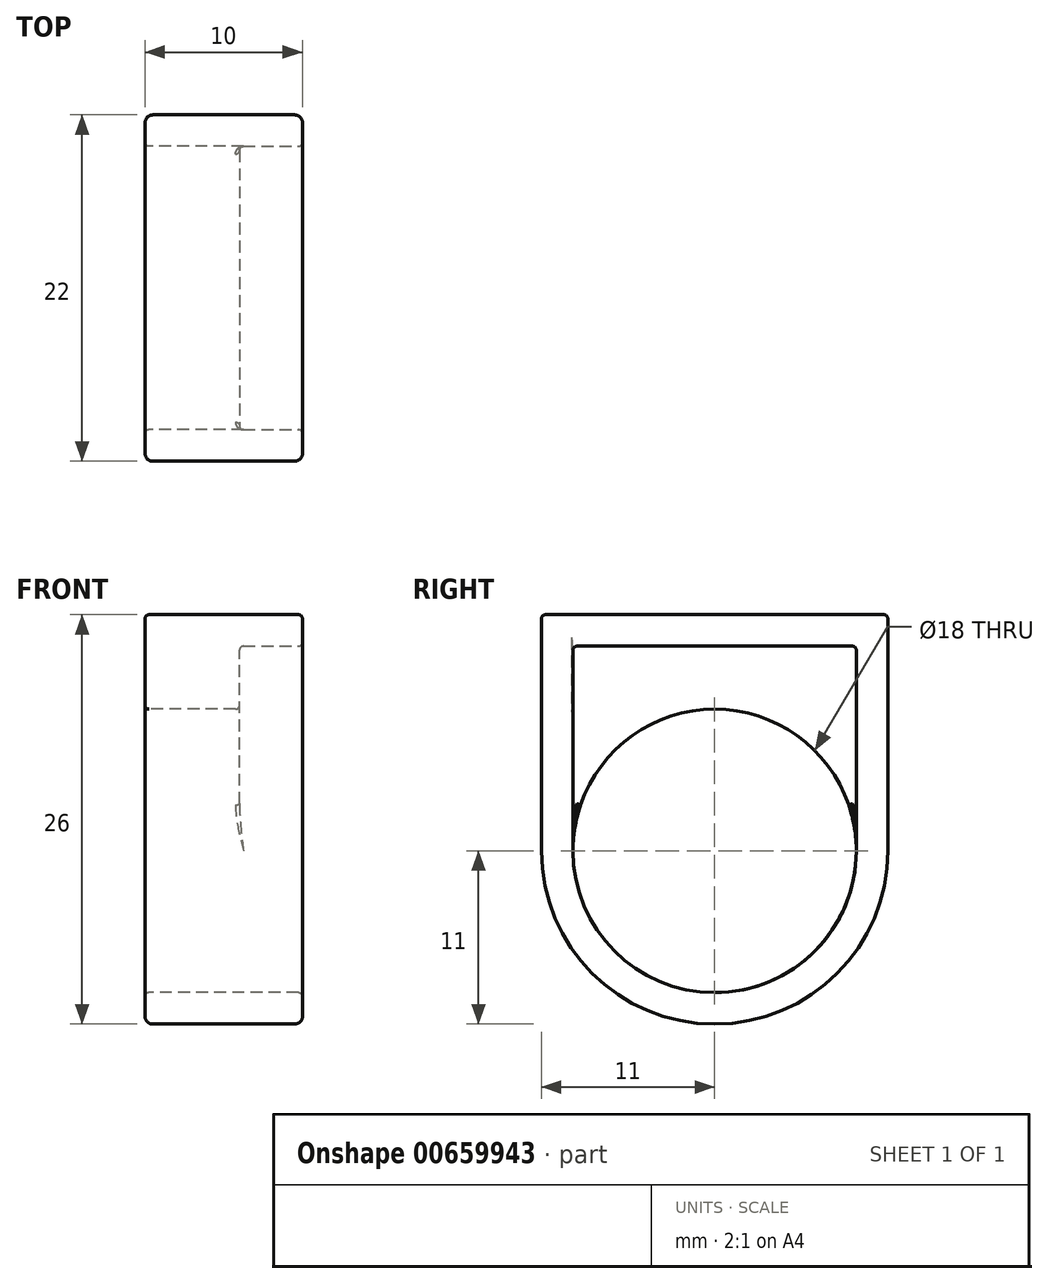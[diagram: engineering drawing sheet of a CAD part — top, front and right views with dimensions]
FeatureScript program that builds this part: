
annotation { "Feature Type Name" : "Feature", "Feature Type Description" : "" }
export const myFeature = defineFeature(function(context is Context, id is Id, definition is map)
    precondition{}
    {
        {
            var Q0;
            Q0=qCreatedBy(makeId("Right.planeOp"),FACE);
            var sketch = newSketch(context, id + "F0", { "sketchPlane" : qUnion([Q0])});
            skCircle(sketch, "E0", {"center": v(0, 0) * mm, "radius": 9 * mm});
            skArc(sketch, "E1", {"start": v(-11, 0) * mm, "mid": v(0, -11) * mm, "end": v(11, 0) * mm});
            skLineSegment(sketch, "E2", {"start": v(11, 0) * mm, "end": v(11, 15) * mm});
            skLineSegment(sketch, "E3", {"start": v(-11, 0) * mm, "end": v(-11, 15) * mm});
            skLineSegment(sketch, "E4", {"start": v(-11, 15) * mm, "end": v(11, 15) * mm});
            skSolve(sketch);
        }
        {
            var Q0;
            Q0 = qSketchRegion(id + "F0", true);
            extrude(context, id + "F1", {"entities" : qUnion([Q0]), "endBound" : BoundingType.SYMMETRIC, "depth" : 10 * mm, "offsetDistance" : 25 * mm});
        }
        {
            var Q0;
            Q0=makeQuery(id+"F1.opExtrude","CAP_FACE",FACE,{"disambiguationData":[OSD([sQuery(id+"F0.wireOp",EDGE,"E0"),sQuery(id+"F0.wireOp",EDGE,"E1"),sQuery(id+"F0.wireOp",EDGE,"E2"),sQuery(id+"F0.wireOp",EDGE,"E3"),sQuery(id+"F0.wireOp",EDGE,"E4")])],"isStart":false});
            var sketch = newSketch(context, id + "F2", { "sketchPlane" : qUnion([Q0])});
            skLineSegment(sketch, "E5.0", {"start": v(9, 13) * mm, "end": v(-9, 13) * mm});
            skLineSegment(sketch, "E5.1", {"start": v(9, 0) * mm, "end": v(9, 13) * mm});
            skArc(sketch, "E5.2", {"start": v(-9, 0) * mm, "mid": v(0, -9) * mm, "end": v(9, 0) * mm});
            skLineSegment(sketch, "E5.3", {"start": v(-9, 13) * mm, "end": v(-9, 0) * mm});
            skSolve(sketch);
        }
        {
            var Q0;
            Q0 = qSketchRegion(id + "F2", true);
            extrude(context, id + "F3", {"entities" : qUnion([Q0]), "operationType" : NewBodyOperationType.REMOVE, "endBound" : BoundingType.SYMMETRIC, "oppositeDirection" : true, "depth" : 8 * mm, "offsetDistance" : 25 * mm});
        }
        {
            var Q0;
            Q0=makeQuery(id+"F1.opExtrude","CAP_EDGE",EDGE,{"disambiguationData":[OSD([sQuery(id+"F0.wireOp",EDGE,"E3")])],"isStart":false});
            var Q1;
            Q1=makeQuery(id+"F1.opExtrude","CAP_EDGE",EDGE,{"disambiguationData":[OSD([sQuery(id+"F0.wireOp",EDGE,"E3")])],"isStart":true});
            fillet(context, id + "F4", {"entities" : qUnion([Q0, Q1]), "radius" : 0.5 * mm, "tangentPropagation" : true, "allowEdgeOverflow" : false});
        }
        {
            var Q0;
            Q0=makeQuery(id+"F1.opExtrude","CAP_EDGE",EDGE,{"disambiguationData":[OSD([sQuery(id+"F0.wireOp",EDGE,"E0")])],"isStart":false});
            var Q1;
            Q1=makeQuery(id+"F1.opExtrude","SWEPT_EDGE",EDGE,{"disambiguationData":[OSD([sQuery(id+"F0.wireOp",EDGE,"E1"),sQuery(id+"F0.wireOp",EDGE,"E3")])]});
            var Q2;
            Q2=makeQuery(id+"F3.boolean.opBoolean","INTERSECT",EDGE,{"derivedFrom":[makeQuery(id+"F1.opExtrude","CAP_FACE",FACE,{"disambiguationData":[OSD([sQuery(id+"F0.wireOp",EDGE,"E0"),sQuery(id+"F0.wireOp",EDGE,"E1"),sQuery(id+"F0.wireOp",EDGE,"E2"),sQuery(id+"F0.wireOp",EDGE,"E3"),sQuery(id+"F0.wireOp",EDGE,"E4")])],"isStart":false}),makeQuery(id+"F3.opExtrude","SWEPT_FACE",FACE,{"disambiguationData":[OSD([sQuery(id+"F2.wireOp",EDGE,"E5.0")])]})]});
            var Q3;
            {var subQ0=sQuery(id+"F0.wireOp",EDGE,"E1");Q3=makeQuery(id+"F4.opFillet","BLEND_EDGE",EDGE,{"blendedFrom":[makeQuery(id+"F1.opExtrude","CAP_EDGE",EDGE,{"disambiguationData":[OSD([subQ0])],"isStart":false}),makeQuery(id+"F1.opExtrude","CAP_FACE",FACE,{"disambiguationData":[OSD([sQuery(id+"F0.wireOp",EDGE,"E0"),subQ0,sQuery(id+"F0.wireOp",EDGE,"E2"),sQuery(id+"F0.wireOp",EDGE,"E3"),sQuery(id+"F0.wireOp",EDGE,"E4")])],"isStart":false})],"blendedInto":[makeQuery(id+"F1.opExtrude","CAP_FACE",FACE,{"disambiguationData":[OSD([sQuery(id+"F0.wireOp",EDGE,"E0"),subQ0,sQuery(id+"F0.wireOp",EDGE,"E2"),sQuery(id+"F0.wireOp",EDGE,"E3"),sQuery(id+"F0.wireOp",EDGE,"E4")])],"isStart":false})]});}
            var Q4;
            Q4=makeQuery(id+"F3.boolean.opBoolean","INTERSECT",EDGE,{"derivedFrom":[makeQuery(id+"F1.opExtrude","SWEPT_FACE",FACE,{"disambiguationData":[OSD([sQuery(id+"F0.wireOp",EDGE,"E0")])]}),makeQuery(id+"F3.opExtrude","CAP_FACE",FACE,{"disambiguationData":[OSD([sQuery(id+"F2.wireOp",EDGE,"E5.0"),sQuery(id+"F2.wireOp",EDGE,"E5.1"),sQuery(id+"F2.wireOp",EDGE,"E5.2"),sQuery(id+"F2.wireOp",EDGE,"E5.3")])],"isStart":false})]});
            var Q5;
            Q5=makeQuery(id+"F3.boolean.opBoolean","COPY",EDGE,{"derivedFrom":makeQuery(id+"F3.opExtrude","SWEPT_EDGE",EDGE,{"disambiguationData":[OSD([sQuery(id+"F0.wireOp",EDGE,"E0"),sQuery(id+"F2.wireOp",EDGE,"E5.1"),sQuery(id+"F2.wireOp",EDGE,"E5.2")])]})});
            var Q6;
            Q6=makeQuery(id+"F1.opExtrude","CAP_EDGE",EDGE,{"disambiguationData":[OSD([sQuery(id+"F0.wireOp",EDGE,"E0")])],"isStart":true});
            var Q7;
            Q7=makeQuery(id+"F1.opExtrude","SWEPT_EDGE",EDGE,{"disambiguationData":[OSD([sQuery(id+"F0.wireOp",EDGE,"E2"),sQuery(id+"F0.wireOp",EDGE,"E4")])]});
            var Q8;
            Q8=makeQuery(id+"F1.opExtrude","SWEPT_EDGE",EDGE,{"disambiguationData":[OSD([sQuery(id+"F0.wireOp",EDGE,"E3"),sQuery(id+"F0.wireOp",EDGE,"E4")])]});
            var Q9;
            Q9=makeQuery(id+"F1.opExtrude","CAP_EDGE",EDGE,{"disambiguationData":[OSD([sQuery(id+"F0.wireOp",EDGE,"E4")])],"isStart":false});
            var Q10;
            Q10=makeQuery(id+"F1.opExtrude","CAP_EDGE",EDGE,{"disambiguationData":[OSD([sQuery(id+"F0.wireOp",EDGE,"E4")])],"isStart":true});
            var Q11;
            Q11=makeQuery(id+"F3.boolean.opBoolean","INTERSECT",EDGE,{"derivedFrom":[makeQuery(id+"F1.opExtrude","CAP_FACE",FACE,{"disambiguationData":[OSD([sQuery(id+"F0.wireOp",EDGE,"E0"),sQuery(id+"F0.wireOp",EDGE,"E1"),sQuery(id+"F0.wireOp",EDGE,"E2"),sQuery(id+"F0.wireOp",EDGE,"E3"),sQuery(id+"F0.wireOp",EDGE,"E4")])],"isStart":false}),makeQuery(id+"F3.opExtrude","SWEPT_FACE",FACE,{"disambiguationData":[OSD([sQuery(id+"F2.wireOp",EDGE,"E5.3")])]})]});
            var Q12;
            Q12=makeQuery(id+"F3.boolean.opBoolean","INTERSECT",EDGE,{"derivedFrom":[makeQuery(id+"F1.opExtrude","CAP_FACE",FACE,{"disambiguationData":[OSD([sQuery(id+"F0.wireOp",EDGE,"E0"),sQuery(id+"F0.wireOp",EDGE,"E1"),sQuery(id+"F0.wireOp",EDGE,"E2"),sQuery(id+"F0.wireOp",EDGE,"E3"),sQuery(id+"F0.wireOp",EDGE,"E4")])],"isStart":false}),makeQuery(id+"F3.opExtrude","SWEPT_FACE",FACE,{"disambiguationData":[OSD([sQuery(id+"F2.wireOp",EDGE,"E5.1")])]})]});
            var Q13;
            Q13=makeQuery(id+"F4.opFillet","BLEND_EDGE",EDGE,{"blendedFrom":[makeQuery(id+"F1.opExtrude","CAP_EDGE",EDGE,{"disambiguationData":[OSD([sQuery(id+"F0.wireOp",EDGE,"E1")])],"isStart":false}),makeQuery(id+"F1.opExtrude","CAP_EDGE",EDGE,{"disambiguationData":[OSD([sQuery(id+"F0.wireOp",EDGE,"E3")])],"isStart":false})],"blendedInto":[]});
            var Q14;
            {var subQ0=sQuery(id+"F0.wireOp",EDGE,"E1");Q14=makeQuery(id+"F4.opFillet","BLEND_EDGE",EDGE,{"blendedFrom":[makeQuery(id+"F1.opExtrude","CAP_EDGE",EDGE,{"disambiguationData":[OSD([subQ0])],"isStart":false}),makeQuery(id+"F1.opExtrude","SWEPT_FACE",FACE,{"disambiguationData":[OSD([subQ0])]})],"blendedInto":[makeQuery(id+"F1.opExtrude","SWEPT_FACE",FACE,{"disambiguationData":[OSD([subQ0])]})]});}
            var Q15;
            {var subQ0=sQuery(id+"F0.wireOp",EDGE,"E3");Q15=makeQuery(id+"F4.opFillet","BLEND_EDGE",EDGE,{"blendedFrom":[makeQuery(id+"F1.opExtrude","CAP_EDGE",EDGE,{"disambiguationData":[OSD([subQ0])],"isStart":false}),makeQuery(id+"F1.opExtrude","SWEPT_FACE",FACE,{"disambiguationData":[OSD([subQ0])]})],"blendedInto":[makeQuery(id+"F1.opExtrude","SWEPT_FACE",FACE,{"disambiguationData":[OSD([subQ0])]})]});}
            var Q16;
            Q16=makeQuery(id+"F3.boolean.opBoolean","COPY",EDGE,{"derivedFrom":makeQuery(id+"F3.opExtrude","CAP_EDGE",EDGE,{"disambiguationData":[OSD([sQuery(id+"F2.wireOp",EDGE,"E5.0")])],"isStart":false})});
            var Q17;
            Q17=makeQuery(id+"F3.boolean.opBoolean","COPY",EDGE,{"derivedFrom":makeQuery(id+"F3.opExtrude","CAP_EDGE",EDGE,{"disambiguationData":[OSD([sQuery(id+"F2.wireOp",EDGE,"E5.1")])],"isStart":false})});
            var Q18;
            Q18=makeQuery(id+"F3.boolean.opBoolean","COPY",EDGE,{"derivedFrom":makeQuery(id+"F3.opExtrude","SWEPT_EDGE",EDGE,{"disambiguationData":[OSD([sQuery(id+"F2.wireOp",EDGE,"E5.0"),sQuery(id+"F2.wireOp",EDGE,"E5.1")])]})});
            var Q19;
            Q19=makeQuery(id+"F3.boolean.opBoolean","COPY",EDGE,{"derivedFrom":makeQuery(id+"F3.opExtrude","CAP_EDGE",EDGE,{"disambiguationData":[OSD([sQuery(id+"F2.wireOp",EDGE,"E5.3")])],"isStart":false})});
            var Q20;
            Q20=makeQuery(id+"F3.boolean.opBoolean","COPY",EDGE,{"derivedFrom":makeQuery(id+"F3.opExtrude","SWEPT_EDGE",EDGE,{"disambiguationData":[OSD([sQuery(id+"F2.wireOp",EDGE,"E5.0"),sQuery(id+"F2.wireOp",EDGE,"E5.3")])]})});
            var Q21;
            Q21=makeQuery(id+"F3.boolean.opBoolean","COPY",EDGE,{"derivedFrom":makeQuery(id+"F3.opExtrude","SWEPT_EDGE",EDGE,{"disambiguationData":[OSD([sQuery(id+"F0.wireOp",EDGE,"E0"),sQuery(id+"F2.wireOp",EDGE,"E5.2"),sQuery(id+"F2.wireOp",EDGE,"E5.3")])]})});
            var Q22;
            Q22=makeQuery(id+"F4.opFillet","BLEND_EDGE",EDGE,{"blendedFrom":[makeQuery(id+"F1.opExtrude","CAP_EDGE",EDGE,{"disambiguationData":[OSD([sQuery(id+"F0.wireOp",EDGE,"E3")])],"isStart":false}),makeQuery(id+"F1.opExtrude","SWEPT_FACE",FACE,{"disambiguationData":[OSD([sQuery(id+"F0.wireOp",EDGE,"E4")])]})],"blendedInto":[makeQuery(id+"F1.opExtrude","SWEPT_FACE",FACE,{"disambiguationData":[OSD([sQuery(id+"F0.wireOp",EDGE,"E4")])]})]});
            var Q23;
            {var subQ0=sQuery(id+"F0.wireOp",EDGE,"E1");Q23=makeQuery(id+"F4.opFillet","BLEND_EDGE",EDGE,{"blendedFrom":[makeQuery(id+"F1.opExtrude","CAP_EDGE",EDGE,{"disambiguationData":[OSD([subQ0])],"isStart":true}),makeQuery(id+"F1.opExtrude","CAP_FACE",FACE,{"disambiguationData":[OSD([sQuery(id+"F0.wireOp",EDGE,"E0"),subQ0,sQuery(id+"F0.wireOp",EDGE,"E2"),sQuery(id+"F0.wireOp",EDGE,"E3"),sQuery(id+"F0.wireOp",EDGE,"E4")])],"isStart":true})],"blendedInto":[makeQuery(id+"F1.opExtrude","CAP_FACE",FACE,{"disambiguationData":[OSD([sQuery(id+"F0.wireOp",EDGE,"E0"),subQ0,sQuery(id+"F0.wireOp",EDGE,"E2"),sQuery(id+"F0.wireOp",EDGE,"E3"),sQuery(id+"F0.wireOp",EDGE,"E4")])],"isStart":true})]});}
            var Q24;
            Q24=makeQuery(id+"F4.opFillet","BLEND_EDGE",EDGE,{"blendedFrom":[makeQuery(id+"F1.opExtrude","CAP_EDGE",EDGE,{"disambiguationData":[OSD([sQuery(id+"F0.wireOp",EDGE,"E2")])],"isStart":false}),makeQuery(id+"F1.opExtrude","SWEPT_FACE",FACE,{"disambiguationData":[OSD([sQuery(id+"F0.wireOp",EDGE,"E4")])]})],"blendedInto":[makeQuery(id+"F1.opExtrude","SWEPT_FACE",FACE,{"disambiguationData":[OSD([sQuery(id+"F0.wireOp",EDGE,"E4")])]})]});
            var Q25;
            {var subQ0=sQuery(id+"F0.wireOp",EDGE,"E2");Q25=makeQuery(id+"F4.opFillet","BLEND_EDGE",EDGE,{"blendedFrom":[makeQuery(id+"F1.opExtrude","CAP_EDGE",EDGE,{"disambiguationData":[OSD([subQ0])],"isStart":false}),makeQuery(id+"F1.opExtrude","CAP_FACE",FACE,{"disambiguationData":[OSD([sQuery(id+"F0.wireOp",EDGE,"E0"),sQuery(id+"F0.wireOp",EDGE,"E1"),subQ0,sQuery(id+"F0.wireOp",EDGE,"E3"),sQuery(id+"F0.wireOp",EDGE,"E4")])],"isStart":false})],"blendedInto":[makeQuery(id+"F1.opExtrude","CAP_FACE",FACE,{"disambiguationData":[OSD([sQuery(id+"F0.wireOp",EDGE,"E0"),sQuery(id+"F0.wireOp",EDGE,"E1"),subQ0,sQuery(id+"F0.wireOp",EDGE,"E3"),sQuery(id+"F0.wireOp",EDGE,"E4")])],"isStart":false})]});}
            var Q26;
            {var subQ0=sQuery(id+"F0.wireOp",EDGE,"E3");Q26=makeQuery(id+"F4.opFillet","BLEND_EDGE",EDGE,{"blendedFrom":[makeQuery(id+"F1.opExtrude","CAP_EDGE",EDGE,{"disambiguationData":[OSD([subQ0])],"isStart":true}),makeQuery(id+"F1.opExtrude","SWEPT_FACE",FACE,{"disambiguationData":[OSD([subQ0])]})],"blendedInto":[makeQuery(id+"F1.opExtrude","SWEPT_FACE",FACE,{"disambiguationData":[OSD([subQ0])]})]});}
            var Q27;
            {var subQ0=sQuery(id+"F0.wireOp",EDGE,"E1");Q27=makeQuery(id+"F4.opFillet","BLEND_EDGE",EDGE,{"blendedFrom":[makeQuery(id+"F1.opExtrude","CAP_EDGE",EDGE,{"disambiguationData":[OSD([subQ0])],"isStart":true}),makeQuery(id+"F1.opExtrude","SWEPT_FACE",FACE,{"disambiguationData":[OSD([subQ0])]})],"blendedInto":[makeQuery(id+"F1.opExtrude","SWEPT_FACE",FACE,{"disambiguationData":[OSD([subQ0])]})]});}
            var Q28;
            {var subQ0=sQuery(id+"F0.wireOp",EDGE,"E3");Q28=makeQuery(id+"F4.opFillet","BLEND_EDGE",EDGE,{"blendedFrom":[makeQuery(id+"F1.opExtrude","CAP_EDGE",EDGE,{"disambiguationData":[OSD([subQ0])],"isStart":false}),makeQuery(id+"F1.opExtrude","CAP_FACE",FACE,{"disambiguationData":[OSD([sQuery(id+"F0.wireOp",EDGE,"E0"),sQuery(id+"F0.wireOp",EDGE,"E1"),sQuery(id+"F0.wireOp",EDGE,"E2"),subQ0,sQuery(id+"F0.wireOp",EDGE,"E4")])],"isStart":false})],"blendedInto":[makeQuery(id+"F1.opExtrude","CAP_FACE",FACE,{"disambiguationData":[OSD([sQuery(id+"F0.wireOp",EDGE,"E0"),sQuery(id+"F0.wireOp",EDGE,"E1"),sQuery(id+"F0.wireOp",EDGE,"E2"),subQ0,sQuery(id+"F0.wireOp",EDGE,"E4")])],"isStart":false})]});}
            var Q29;
            Q29=makeQuery(id+"F1.opExtrude","SWEPT_EDGE",EDGE,{"disambiguationData":[OSD([sQuery(id+"F0.wireOp",EDGE,"E1"),sQuery(id+"F0.wireOp",EDGE,"E2")])]});
            var Q30;
            Q30=makeQuery(id+"F4.opFillet","BLEND_EDGE",EDGE,{"blendedFrom":[makeQuery(id+"F1.opExtrude","CAP_EDGE",EDGE,{"disambiguationData":[OSD([sQuery(id+"F0.wireOp",EDGE,"E1")])],"isStart":false}),makeQuery(id+"F1.opExtrude","CAP_EDGE",EDGE,{"disambiguationData":[OSD([sQuery(id+"F0.wireOp",EDGE,"E2")])],"isStart":false})],"blendedInto":[]});
            var Q31;
            {var subQ0=sQuery(id+"F0.wireOp",EDGE,"E2");Q31=makeQuery(id+"F4.opFillet","BLEND_EDGE",EDGE,{"blendedFrom":[makeQuery(id+"F1.opExtrude","CAP_EDGE",EDGE,{"disambiguationData":[OSD([subQ0])],"isStart":false}),makeQuery(id+"F1.opExtrude","SWEPT_FACE",FACE,{"disambiguationData":[OSD([subQ0])]})],"blendedInto":[makeQuery(id+"F1.opExtrude","SWEPT_FACE",FACE,{"disambiguationData":[OSD([subQ0])]})]});}
            var Q32;
            {var subQ0=sQuery(id+"F0.wireOp",EDGE,"E2");Q32=makeQuery(id+"F4.opFillet","BLEND_EDGE",EDGE,{"blendedFrom":[makeQuery(id+"F1.opExtrude","CAP_EDGE",EDGE,{"disambiguationData":[OSD([subQ0])],"isStart":true}),makeQuery(id+"F1.opExtrude","SWEPT_FACE",FACE,{"disambiguationData":[OSD([subQ0])]})],"blendedInto":[makeQuery(id+"F1.opExtrude","SWEPT_FACE",FACE,{"disambiguationData":[OSD([subQ0])]})]});}
            var Q33;
            {var subQ0=sQuery(id+"F0.wireOp",EDGE,"E3");Q33=makeQuery(id+"F4.opFillet","BLEND_EDGE",EDGE,{"blendedFrom":[makeQuery(id+"F1.opExtrude","CAP_EDGE",EDGE,{"disambiguationData":[OSD([subQ0])],"isStart":true}),makeQuery(id+"F1.opExtrude","CAP_FACE",FACE,{"disambiguationData":[OSD([sQuery(id+"F0.wireOp",EDGE,"E0"),sQuery(id+"F0.wireOp",EDGE,"E1"),sQuery(id+"F0.wireOp",EDGE,"E2"),subQ0,sQuery(id+"F0.wireOp",EDGE,"E4")])],"isStart":true})],"blendedInto":[makeQuery(id+"F1.opExtrude","CAP_FACE",FACE,{"disambiguationData":[OSD([sQuery(id+"F0.wireOp",EDGE,"E0"),sQuery(id+"F0.wireOp",EDGE,"E1"),sQuery(id+"F0.wireOp",EDGE,"E2"),subQ0,sQuery(id+"F0.wireOp",EDGE,"E4")])],"isStart":true})]});}
            var Q34;
            Q34=makeQuery(id+"F4.opFillet","BLEND_EDGE",EDGE,{"blendedFrom":[makeQuery(id+"F1.opExtrude","CAP_EDGE",EDGE,{"disambiguationData":[OSD([sQuery(id+"F0.wireOp",EDGE,"E3")])],"isStart":true}),makeQuery(id+"F1.opExtrude","SWEPT_FACE",FACE,{"disambiguationData":[OSD([sQuery(id+"F0.wireOp",EDGE,"E4")])]})],"blendedInto":[makeQuery(id+"F1.opExtrude","SWEPT_FACE",FACE,{"disambiguationData":[OSD([sQuery(id+"F0.wireOp",EDGE,"E4")])]})]});
            var Q35;
            Q35=makeQuery(id+"F4.opFillet","BLEND_EDGE",EDGE,{"blendedFrom":[makeQuery(id+"F1.opExtrude","CAP_EDGE",EDGE,{"disambiguationData":[OSD([sQuery(id+"F0.wireOp",EDGE,"E1")])],"isStart":true}),makeQuery(id+"F1.opExtrude","CAP_EDGE",EDGE,{"disambiguationData":[OSD([sQuery(id+"F0.wireOp",EDGE,"E3")])],"isStart":true})],"blendedInto":[]});
            var Q36;
            {var subQ0=sQuery(id+"F0.wireOp",EDGE,"E2");Q36=makeQuery(id+"F4.opFillet","BLEND_EDGE",EDGE,{"blendedFrom":[makeQuery(id+"F1.opExtrude","CAP_EDGE",EDGE,{"disambiguationData":[OSD([subQ0])],"isStart":true}),makeQuery(id+"F1.opExtrude","CAP_FACE",FACE,{"disambiguationData":[OSD([sQuery(id+"F0.wireOp",EDGE,"E0"),sQuery(id+"F0.wireOp",EDGE,"E1"),subQ0,sQuery(id+"F0.wireOp",EDGE,"E3"),sQuery(id+"F0.wireOp",EDGE,"E4")])],"isStart":true})],"blendedInto":[makeQuery(id+"F1.opExtrude","CAP_FACE",FACE,{"disambiguationData":[OSD([sQuery(id+"F0.wireOp",EDGE,"E0"),sQuery(id+"F0.wireOp",EDGE,"E1"),subQ0,sQuery(id+"F0.wireOp",EDGE,"E3"),sQuery(id+"F0.wireOp",EDGE,"E4")])],"isStart":true})]});}
            var Q37;
            Q37=makeQuery(id+"F4.opFillet","BLEND_EDGE",EDGE,{"blendedFrom":[makeQuery(id+"F1.opExtrude","CAP_EDGE",EDGE,{"disambiguationData":[OSD([sQuery(id+"F0.wireOp",EDGE,"E2")])],"isStart":true}),makeQuery(id+"F1.opExtrude","SWEPT_FACE",FACE,{"disambiguationData":[OSD([sQuery(id+"F0.wireOp",EDGE,"E4")])]})],"blendedInto":[makeQuery(id+"F1.opExtrude","SWEPT_FACE",FACE,{"disambiguationData":[OSD([sQuery(id+"F0.wireOp",EDGE,"E4")])]})]});
            var Q38;
            Q38=makeQuery(id+"F4.opFillet","BLEND_EDGE",EDGE,{"blendedFrom":[makeQuery(id+"F1.opExtrude","CAP_EDGE",EDGE,{"disambiguationData":[OSD([sQuery(id+"F0.wireOp",EDGE,"E1")])],"isStart":true}),makeQuery(id+"F1.opExtrude","CAP_EDGE",EDGE,{"disambiguationData":[OSD([sQuery(id+"F0.wireOp",EDGE,"E2")])],"isStart":true})],"blendedInto":[]});
            fillet(context, id + "F5", {"entities" : qUnion([Q0, Q1, Q2, Q3, Q4, Q5, Q6, Q7, Q8, Q9, Q10, Q11, Q12, Q13, Q14, Q15, Q16, Q17, Q18, Q19, Q20, Q21, Q22, Q23, Q24, Q25, Q26, Q27, Q28, Q29, Q30, Q31, Q32, Q33, Q34, Q35, Q36, Q37, Q38]), "radius" : .25 * mm, "tangentPropagation" : true, "allowEdgeOverflow" : false});
        }
    });
